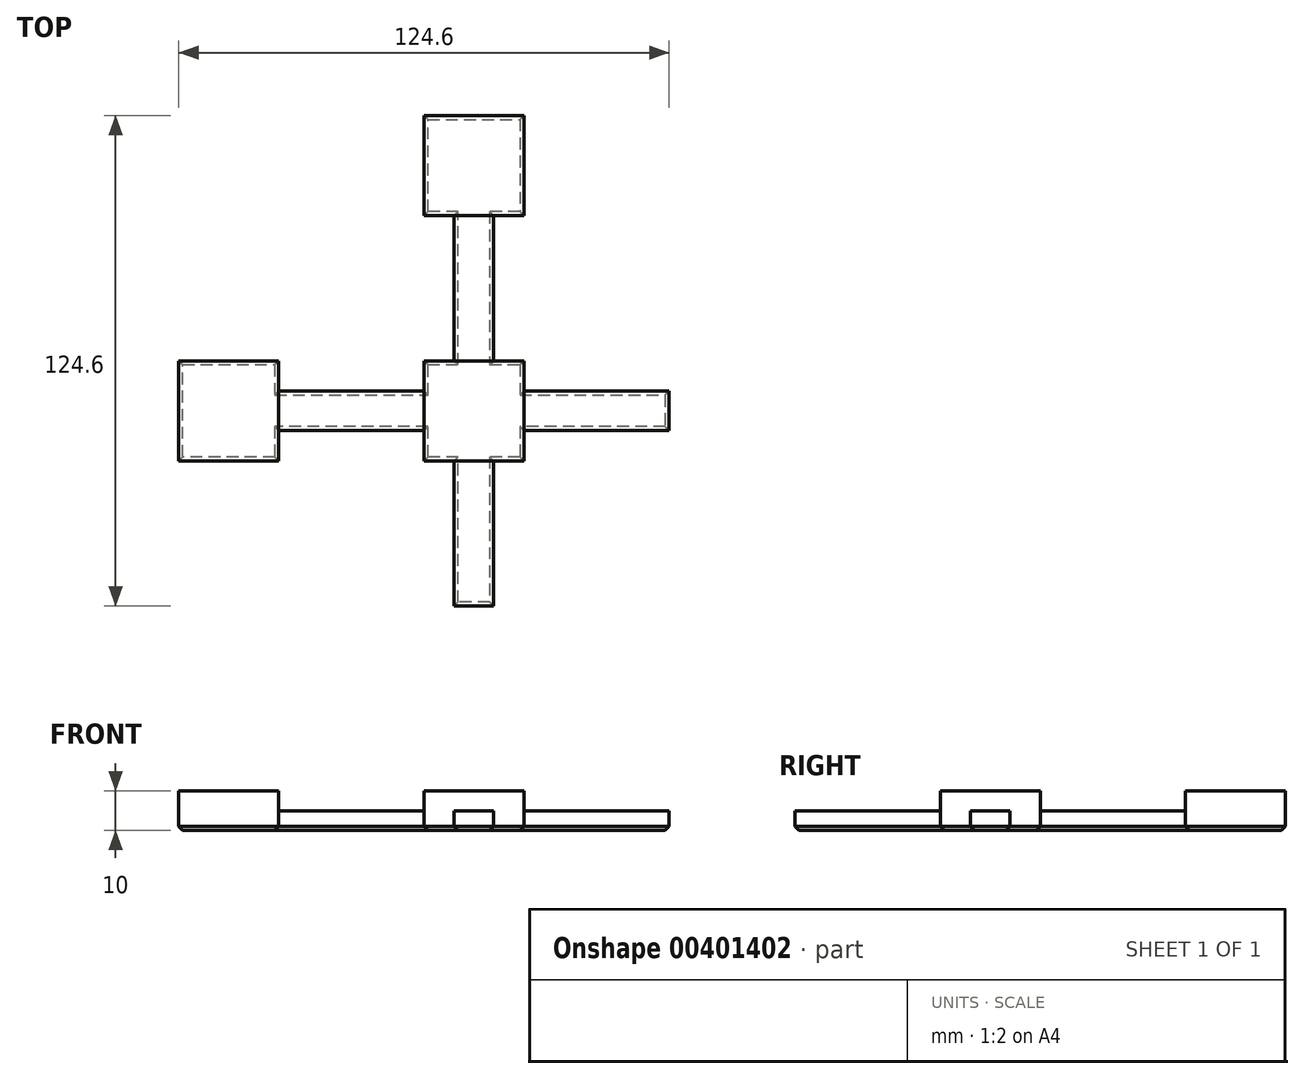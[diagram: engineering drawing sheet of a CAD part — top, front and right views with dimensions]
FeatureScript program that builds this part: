
annotation { "Feature Type Name" : "Feature", "Feature Type Description" : "" }
export const myFeature = defineFeature(function(context is Context, id is Id, definition is map)
    precondition{}
    {
        {
            var Q0;
            Q0=qCreatedBy(makeId("Top.planeOp"),FACE);
            var sketch = newSketch(context, id + "F0", { "sketchPlane" : qUnion([Q0])});
            skLineSegment(sketch, "E0.bottom", {"start": v(-12.7, 75) * mm, "end": v(12.7, 75) * mm});
            skLineSegment(sketch, "E0.top", {"start": v(-12.7, -75) * mm, "end": v(12.7, -75) * mm});
            skLineSegment(sketch, "E0.left", {"start": v(-75, 12.7) * mm, "end": v(-75, -12.7) * mm});
            skLineSegment(sketch, "E0.right", {"start": v(75, 12.7) * mm, "end": v(75, -12.7) * mm});
            skPoint(sketch, "E0.middle", {"position": v(0, 0) * mm});
            skLineSegment(sketch, "E1.left", {"start": v(-12.7, 75) * mm, "end": v(-12.7, 49.6) * mm});
            skLineSegment(sketch, "E1.right", {"start": v(12.7, 75) * mm, "end": v(12.7, 49.6) * mm});
            skLineSegment(sketch, "E2.bottom", {"start": v(-75, 12.7) * mm, "end": v(-49.6, 12.7) * mm});
            skLineSegment(sketch, "E2.top", {"start": v(-75, -12.7) * mm, "end": v(-49.6, -12.7) * mm});
            skLineSegment(sketch, "E2.left", {"start": v(-75, 5) * mm, "end": v(-75, -5) * mm});
            skLineSegment(sketch, "E3.bottom", {"start": v(-5, 75) * mm, "end": v(5, 75) * mm});
            skLineSegment(sketch, "E3.top", {"start": v(-5, -75) * mm, "end": v(5, -75) * mm});
            skLineSegment(sketch, "E3.left", {"start": v(-5, 49.6) * mm, "end": v(-5, 12.7) * mm});
            skLineSegment(sketch, "E3.right", {"start": v(5, 49.6) * mm, "end": v(5, 12.7) * mm});
            skLineSegment(sketch, "E4.bottom", {"start": v(-49.6, 5) * mm, "end": v(-5, 5) * mm});
            skLineSegment(sketch, "E4.top", {"start": v(-49.6, -5) * mm, "end": v(-12.7, -5) * mm});
            skLineSegment(sketch, "E4.right", {"start": v(75, 5) * mm, "end": v(75, -5) * mm});
            skLineSegment(sketch, "E5", {"start": v(-49.6, 12.7) * mm, "end": v(-49.6, -12.7) * mm});
            skLineSegment(sketch, "E6", {"start": v(49.6, 12.7) * mm, "end": v(49.6, -12.7) * mm});
            skLineSegment(sketch, "E7", {"start": v(-12.7, 49.6) * mm, "end": v(12.7, 49.6) * mm});
            skLineSegment(sketch, "E8", {"start": v(-12.7, -49.6) * mm, "end": v(12.7, -49.6) * mm});
            skPoint(sketch, "E4.left.end.orphan", {"position": v(-75, -5) * mm});
            skPoint(sketch, "E4.left.start.orphan", {"position": v(-75, 5) * mm});
            skPoint(sketch, "E9.orphan", {"position": v(-75, 75) * mm});
            skPoint(sketch, "E10.orphan", {"position": v(75, 75) * mm});
            skPoint(sketch, "E11.orphan", {"position": v(75, -75) * mm});
            skPoint(sketch, "E12.orphan", {"position": v(-75, -75) * mm});
            skLineSegment(sketch, "E13.trimOffspring", {"start": v(-12.7, -12.7) * mm, "end": v(12.7, -12.7) * mm});
            skLineSegment(sketch, "E14.trimOffspring", {"start": v(-12.7, 12.7) * mm, "end": v(12.7, 12.7) * mm});
            skLineSegment(sketch, "E15.trimOffspring", {"start": v(-12.7, 12.7) * mm, "end": v(-12.7, -12.7) * mm});
            skLineSegment(sketch, "E16.trimOffspring", {"start": v(12.7, 12.7) * mm, "end": v(12.7, -12.7) * mm});
            skLineSegment(sketch, "E17.trimOffspring", {"start": v(49.6, 12.7) * mm, "end": v(75, 12.7) * mm});
            skLineSegment(sketch, "E18.trimOffspring", {"start": v(49.6, -12.7) * mm, "end": v(75, -12.7) * mm});
            skLineSegment(sketch, "E19.trimOffspring", {"start": v(12.7, -49.6) * mm, "end": v(12.7, -75) * mm});
            skLineSegment(sketch, "E20.trimOffspring", {"start": v(-12.7, -49.6) * mm, "end": v(-12.7, -75) * mm});
            skLineSegment(sketch, "E21.trimOffspring", {"start": v(12.7, -5) * mm, "end": v(49.6, -5) * mm});
            skLineSegment(sketch, "E22.trimOffspring", {"start": v(12.7, 5) * mm, "end": v(49.6, 5) * mm});
            skLineSegment(sketch, "E23.trimOffspring", {"start": v(-5, -12.7) * mm, "end": v(-5, -49.6) * mm});
            skLineSegment(sketch, "E24.trimOffspring", {"start": v(5, -12.7) * mm, "end": v(5, -49.6) * mm});
            skSolve(sketch);
        }
        {
            var Q0;
            {var subQ5=sQuery(id+"F0.wireOp",EDGE,"E4.right");Q0=makeQuery(id+"F0.imprint","IMPRINT",FACE,{"disambiguationData":[TD([[makeQuery(id+"F0.imprint","IMPRINT",EDGE,{"derivedFrom":subQ5}),-1.0]])]});}
            var Q1;
            {var subQ0=sQuery(id+"F0.wireOp",EDGE,"E21.trimOffspring");Q1=makeQuery(id+"F0.imprint","IMPRINT",FACE,{"disambiguationData":[TD([[makeQuery(id+"F0.imprint","IMPRINT",EDGE,{"derivedFrom":subQ0}),1.0]])]});}
            var Q2;
            {var subQ4=sQuery(id+"F0.wireOp",EDGE,"E15.trimOffspring");var subQ6=sQuery(id+"F0.wireOp",EDGE,"E13.trimOffspring");var subQ7=makeQuery(id+"F0.imprint","INTERSECT",VERTEX,{"derivedFrom":[subQ6,subQ4]});Q2=makeQuery(id+"F0.imprint","IMPRINT",FACE,{"disambiguationData":[TD([[makeQuery(id+"F0.imprint","IMPRINT",EDGE,{"disambiguationData":[TD([[subQ7,-1.0]])],"derivedFrom":subQ6}),1.0]])]});}
            var Q3;
            {var subQ0=sQuery(id+"F0.wireOp",EDGE,"E23.trimOffspring");Q3=makeQuery(id+"F0.imprint","IMPRINT",FACE,{"disambiguationData":[TD([[makeQuery(id+"F0.imprint","IMPRINT",EDGE,{"derivedFrom":subQ0}),1.0]])]});}
            var Q4;
            {var subQ2=sQuery(id+"F0.wireOp",EDGE,"E3.top");Q4=makeQuery(id+"F0.imprint","IMPRINT",FACE,{"disambiguationData":[TD([[makeQuery(id+"F0.imprint","IMPRINT",EDGE,{"derivedFrom":subQ2}),1.0]])]});}
            var Q5;
            {var subQ5=sQuery(id+"F0.wireOp",EDGE,"E4.top");Q5=makeQuery(id+"F0.imprint","IMPRINT",FACE,{"disambiguationData":[TD([[makeQuery(id+"F0.imprint","IMPRINT",EDGE,{"derivedFrom":subQ5}),1.0]])]});}
            var Q6;
            {var subQ2=sQuery(id+"F0.wireOp",EDGE,"E2.bottom");Q6=makeQuery(id+"F0.imprint","IMPRINT",FACE,{"disambiguationData":[TD([[makeQuery(id+"F0.imprint","IMPRINT",EDGE,{"derivedFrom":subQ2}),-1.0]])]});}
            var Q7;
            {var subQ0=sQuery(id+"F0.wireOp",EDGE,"E3.left");Q7=makeQuery(id+"F0.imprint","IMPRINT",FACE,{"disambiguationData":[TD([[makeQuery(id+"F0.imprint","IMPRINT",EDGE,{"derivedFrom":subQ0}),1.0]])]});}
            var Q8;
            {var subQ0=sQuery(id+"F0.wireOp",EDGE,"E1.left");Q8=makeQuery(id+"F0.imprint","IMPRINT",FACE,{"disambiguationData":[TD([[makeQuery(id+"F0.imprint","IMPRINT",EDGE,{"derivedFrom":subQ0}),1.0]])]});}
            extrude(context, id + "F1", {"entities" : qUnion([Q0, Q1, Q2, Q3, Q4, Q5, Q6, Q7, Q8]), "depth" : 5 * mm});
        }
        {
            var Q0;
            {var subQ2=sQuery(id+"F0.wireOp",EDGE,"E2.bottom");Q0=makeQuery(id+"F0.imprint","IMPRINT",FACE,{"disambiguationData":[TD([[makeQuery(id+"F0.imprint","IMPRINT",EDGE,{"derivedFrom":subQ2}),-1.0]])]});}
            var Q1;
            {var subQ0=sQuery(id+"F0.wireOp",EDGE,"E1.left");Q1=makeQuery(id+"F0.imprint","IMPRINT",FACE,{"disambiguationData":[TD([[makeQuery(id+"F0.imprint","IMPRINT",EDGE,{"derivedFrom":subQ0}),1.0]])]});}
            var Q2;
            {var subQ5=sQuery(id+"F0.wireOp",EDGE,"E4.right");Q2=makeQuery(id+"F0.imprint","IMPRINT",FACE,{"disambiguationData":[TD([[makeQuery(id+"F0.imprint","IMPRINT",EDGE,{"derivedFrom":subQ5}),-1.0]])]});}
            var Q3;
            {var subQ4=sQuery(id+"F0.wireOp",EDGE,"E15.trimOffspring");var subQ6=sQuery(id+"F0.wireOp",EDGE,"E13.trimOffspring");var subQ7=makeQuery(id+"F0.imprint","INTERSECT",VERTEX,{"derivedFrom":[subQ6,subQ4]});Q3=makeQuery(id+"F0.imprint","IMPRINT",FACE,{"disambiguationData":[TD([[makeQuery(id+"F0.imprint","IMPRINT",EDGE,{"disambiguationData":[TD([[subQ7,-1.0]])],"derivedFrom":subQ6}),1.0]])]});}
            var Q4;
            {var subQ2=sQuery(id+"F0.wireOp",EDGE,"E3.top");Q4=makeQuery(id+"F0.imprint","IMPRINT",FACE,{"disambiguationData":[TD([[makeQuery(id+"F0.imprint","IMPRINT",EDGE,{"derivedFrom":subQ2}),1.0]])]});}
            extrude(context, id + "F2", {"entities" : qUnion([Q0, Q1, Q2, Q3, Q4]), "operationType" : NewBodyOperationType.ADD, "depth" : 10 * mm});
        }
        {
            var Q0;
            Q0=makeQuery(id+"F1.opExtrude","CAP_FACE",FACE,{"disambiguationData":[OSD([sQuery(id+"F0.wireOp",EDGE,"E0.left"),sQuery(id+"F0.wireOp",EDGE,"E0.bottom"),sQuery(id+"F0.wireOp",EDGE,"E0.top"),sQuery(id+"F0.wireOp",EDGE,"E1.left"),sQuery(id+"F0.wireOp",EDGE,"E1.right"),sQuery(id+"F0.wireOp",EDGE,"E2.bottom"),sQuery(id+"F0.wireOp",EDGE,"E2.top"),sQuery(id+"F0.wireOp",EDGE,"E2.left"),sQuery(id+"F0.wireOp",EDGE,"E0.right"),sQuery(id+"F0.wireOp",EDGE,"E3.bottom"),sQuery(id+"F0.wireOp",EDGE,"E3.top"),sQuery(id+"F0.wireOp",EDGE,"E3.left"),sQuery(id+"F0.wireOp",EDGE,"E3.right"),sQuery(id+"F0.wireOp",EDGE,"E4.bottom"),sQuery(id+"F0.wireOp",EDGE,"E4.top"),sQuery(id+"F0.wireOp",EDGE,"E4.right"),sQuery(id+"F0.wireOp",EDGE,"E5"),sQuery(id+"F0.wireOp",EDGE,"E6"),sQuery(id+"F0.wireOp",EDGE,"E7"),sQuery(id+"F0.wireOp",EDGE,"E8"),sQuery(id+"F0.wireOp",EDGE,"E13.trimOffspring"),sQuery(id+"F0.wireOp",EDGE,"E14.trimOffspring"),sQuery(id+"F0.wireOp",EDGE,"E15.trimOffspring"),sQuery(id+"F0.wireOp",EDGE,"E16.trimOffspring"),sQuery(id+"F0.wireOp",EDGE,"E17.trimOffspring"),sQuery(id+"F0.wireOp",EDGE,"E18.trimOffspring"),sQuery(id+"F0.wireOp",EDGE,"E19.trimOffspring"),sQuery(id+"F0.wireOp",EDGE,"E20.trimOffspring"),sQuery(id+"F0.wireOp",EDGE,"E21.trimOffspring"),sQuery(id+"F0.wireOp",EDGE,"E22.trimOffspring"),sQuery(id+"F0.wireOp",EDGE,"E23.trimOffspring"),sQuery(id+"F0.wireOp",EDGE,"E24.trimOffspring")])],"isStart":true});
            chamfer(context, id + "F3", {"entities" : qUnion([Q0]), "width" : 1 * mm, "tangentPropagation" : true});
        }
    });
